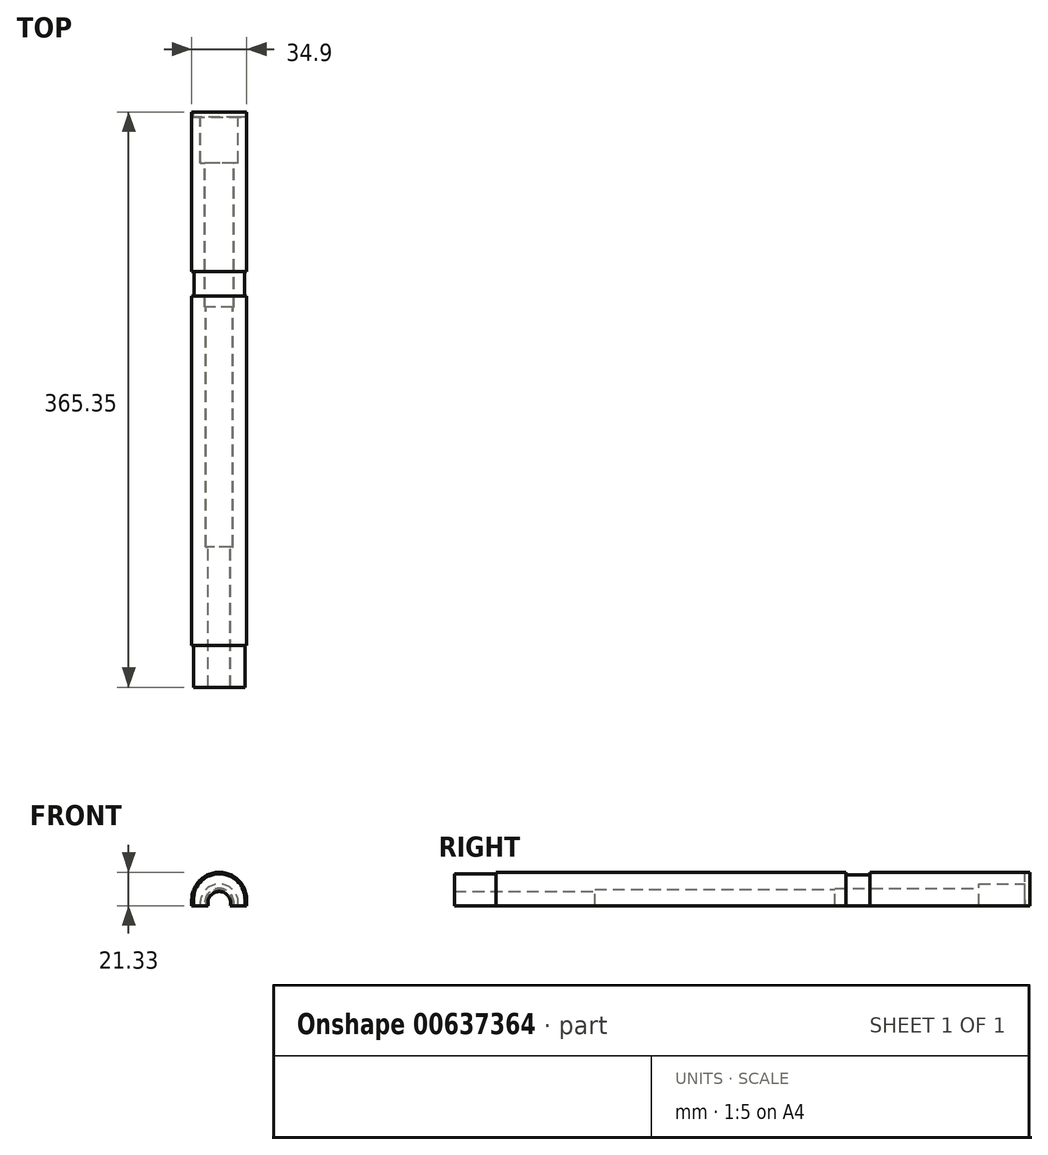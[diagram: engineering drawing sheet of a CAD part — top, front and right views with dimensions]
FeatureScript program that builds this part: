
annotation { "Feature Type Name" : "Feature", "Feature Type Description" : "" }
export const myFeature = defineFeature(function(context is Context, id is Id, definition is map)
    precondition{}
    {
        {
            var Q0;
            Q0=qCreatedBy(makeId("Front.planeOp"),FACE);
            var sketch = newSketch(context, id + "F0", { "sketchPlane" : qUnion([Q0])});
            skLineSegment(sketch, "E0", {"start": v(17.45, -4.64) * mm, "end": v(11.93, -4.64) * mm});
            skLineSegment(sketch, "E1.trimOffspring", {"start": v(-11.93, -4.64) * mm, "end": v(-17.45, -4.64) * mm});
            skLineSegment(sketch, "E2.MirrorCS", {"start": v(17.45, -4.64) * mm, "end": v(17.45, -0.86) * mm});
            skArc(sketch, "E3", {"start": v(17.45, -0.86) * mm, "mid": v(0, 16.7) * mm, "end": v(-17.45, -0.86) * mm});
            skLineSegment(sketch, "E4", {"start": v(-17.45, -0.86) * mm, "end": v(-17.45, -4.64) * mm});
            skArc(sketch, "E5", {"start": v(11.93, -4.64) * mm, "mid": v(0, 9.2) * mm, "end": v(-11.93, -4.64) * mm});
            skSolve(sketch);
        }
        {
            var Q0;
            Q0=makeQuery(id+"F0.imprint","IMPRINT",FACE,{"disambiguationData":[TD([[makeQuery(id+"F0.imprint","IMPRINT",EDGE,{"derivedFrom":sQuery(id+"F0.wireOp",EDGE,"E0")}),-1.0]])]});
            extrude(context, id + "F1", {"entities" : qUnion([Q0]), "depth" : 29.2 * mm, "offsetDistance" : 25.4 * mm});
        }
        {
            var Q0;
            Q0=makeQuery(id+"F1.opExtrude","CAP_FACE",FACE,{"disambiguationData":[OSD([sQuery(id+"F0.wireOp",EDGE,"E0"),sQuery(id+"F0.wireOp",EDGE,"E1.trimOffspring"),sQuery(id+"F0.wireOp",EDGE,"E2.MirrorCS"),sQuery(id+"F0.wireOp",EDGE,"E3"),sQuery(id+"F0.wireOp",EDGE,"E4"),sQuery(id+"F0.wireOp",EDGE,"E5")])],"isStart":false});
            var sketch = newSketch(context, id + "F2", { "sketchPlane" : qUnion([Q0])});
            skArc(sketch, "E6", {"start": v(9.11, -4.64) * mm, "mid": v(0, 6.5) * mm, "end": v(-9.11, -4.64) * mm});
            skLineSegment(sketch, "E7", {"start": v(-17.45, -4.64) * mm, "end": v(-9.11, -4.64) * mm});
            skLineSegment(sketch, "E8", {"start": v(-17.45, -0.86) * mm, "end": v(-17.45, -4.64) * mm});
            skLineSegment(sketch, "E9", {"start": v(17.45, -0.86) * mm, "end": v(17.45, -4.64) * mm});
            skLineSegment(sketch, "E10", {"start": v(17.45, -4.64) * mm, "end": v(9.11, -4.64) * mm});
            skArc(sketch, "E11", {"start": v(17.45, -0.86) * mm, "mid": v(0, 16.7) * mm, "end": v(-17.45, -0.86) * mm});
            skSolve(sketch);
        }
        {
            var Q0;
            {var subQ0=sQuery(id+"F2.wireOp",EDGE,"E6");Q0=makeQuery(id+"F2.imprint","IMPRINT",FACE,{"disambiguationData":[TD([[makeQuery(id+"F2.imprint","IMPRINT",EDGE,{"derivedFrom":subQ0}),-1.0]])]});}
            var Q1;
            {var subQ1=sQuery(id+"F2.wireOp",EDGE,"E8");Q1=makeQuery(id+"F2.imprint","IMPRINT",FACE,{"disambiguationData":[TD([[makeQuery(id+"F2.imprint","IMPRINT",EDGE,{"derivedFrom":subQ1}),1.0]])]});}
            extrude(context, id + "F3", {"entities" : qUnion([Q0, Q1]), "operationType" : NewBodyOperationType.ADD, "depth" : 69.06 * mm, "offsetDistance" : 25.4 * mm});
        }
        {
            var Q0;
            Q0=makeQuery(id+"F3.opExtrude","CAP_FACE",FACE,{"disambiguationData":[OSD([sQuery(id+"F2.wireOp",EDGE,"E6"),sQuery(id+"F2.wireOp",EDGE,"E7"),sQuery(id+"F2.wireOp",EDGE,"E8"),sQuery(id+"F2.wireOp",EDGE,"E9"),sQuery(id+"F2.wireOp",EDGE,"E10"),sQuery(id+"F2.wireOp",EDGE,"E11")])],"isStart":false});
            var sketch = newSketch(context, id + "F4", { "sketchPlane" : qUnion([Q0])});
            skArc(sketch, "E12.0", {"start": v(15.93, -0.85) * mm, "mid": v(0, 15.17) * mm, "end": v(-15.93, -0.85) * mm});
            skLineSegment(sketch, "E13", {"start": v(15.93, -0.85) * mm, "end": v(15.93, -4.64) * mm});
            skLineSegment(sketch, "E14", {"start": v(-15.93, -0.85) * mm, "end": v(-15.9, -4.64) * mm});
            skLineSegment(sketch, "E15", {"start": v(9.11, -4.64) * mm, "end": v(15.93, -4.64) * mm});
            skLineSegment(sketch, "E16", {"start": v(-9.11, -4.64) * mm, "end": v(-15.9, -4.64) * mm});
            skSolve(sketch);
        }
        {
            var Q0;
            Q0=makeQuery(id+"F4.imprint","IMPRINT",FACE,{"disambiguationData":[TD([[makeQuery(id+"F4.imprint","IMPRINT",EDGE,{"derivedFrom":sQuery(id+"F4.wireOp",EDGE,"E12.0")}),1.0]])]});
            extrude(context, id + "F5", {"entities" : qUnion([Q0]), "operationType" : NewBodyOperationType.ADD, "depth" : 15.42 * mm, "offsetDistance" : 25.4 * mm});
        }
        {
            var Q0;
            Q0=makeQuery(id+"F5.opExtrude","CAP_FACE",FACE,{"disambiguationData":[OSD([sQuery(id+"F2.wireOp",EDGE,"E6"),sQuery(id+"F4.wireOp",EDGE,"E12.0"),sQuery(id+"F4.wireOp",EDGE,"E13"),sQuery(id+"F4.wireOp",EDGE,"E14"),sQuery(id+"F4.wireOp",EDGE,"E15"),sQuery(id+"F4.wireOp",EDGE,"E16")])],"isStart":false});
            var sketch = newSketch(context, id + "F6", { "sketchPlane" : qUnion([Q0])});
            skArc(sketch, "E17", {"start": v(9.11, -4.64) * mm, "mid": v(0, 6.5) * mm, "end": v(-9.11, -4.64) * mm});
            skLineSegment(sketch, "E18", {"start": v(-17.45, -4.64) * mm, "end": v(-9.11, -4.64) * mm});
            skLineSegment(sketch, "E19", {"start": v(-17.45, -0.86) * mm, "end": v(-17.45, -4.64) * mm});
            skLineSegment(sketch, "E20", {"start": v(17.45, -0.86) * mm, "end": v(17.45, -4.64) * mm});
            skLineSegment(sketch, "E21", {"start": v(17.45, -4.64) * mm, "end": v(9.11, -4.64) * mm});
            skArc(sketch, "E22", {"start": v(17.45, -0.86) * mm, "mid": v(0, 16.7) * mm, "end": v(-17.45, -0.86) * mm});
            skSolve(sketch);
        }
        {
            var Q0;
            {var subQ1=sQuery(id+"F6.wireOp",EDGE,"E17");Q0=makeQuery(id+"F6.imprint","IMPRINT",FACE,{"disambiguationData":[TD([[makeQuery(id+"F6.imprint","IMPRINT",EDGE,{"derivedFrom":subQ1}),-1.0]])]});}
            var Q1;
            {var subQ3=sQuery(id+"F6.wireOp",EDGE,"E19");Q1=makeQuery(id+"F6.imprint","IMPRINT",FACE,{"disambiguationData":[TD([[makeQuery(id+"F6.imprint","IMPRINT",EDGE,{"derivedFrom":subQ3}),1.0]])]});}
            extrude(context, id + "F7", {"entities" : qUnion([Q0, Q1]), "operationType" : NewBodyOperationType.ADD, "depth" : 6.96 * mm, "offsetDistance" : 25.4 * mm});
        }
        {
            var Q0;
            Q0=makeQuery(id+"F7.opExtrude","CAP_FACE",FACE,{"disambiguationData":[OSD([sQuery(id+"F6.wireOp",EDGE,"E17"),sQuery(id+"F6.wireOp",EDGE,"E18"),sQuery(id+"F6.wireOp",EDGE,"E19"),sQuery(id+"F6.wireOp",EDGE,"E20"),sQuery(id+"F6.wireOp",EDGE,"E21"),sQuery(id+"F6.wireOp",EDGE,"E22")])],"isStart":false});
            var sketch = newSketch(context, id + "F8", { "sketchPlane" : qUnion([Q0])});
            skLineSegment(sketch, "E23", {"start": v(-17.45, -0.86) * mm, "end": v(-17.45, -4.64) * mm});
            skLineSegment(sketch, "E24", {"start": v(17.45, -0.86) * mm, "end": v(17.45, -4.64) * mm});
            skArc(sketch, "E25", {"start": v(17.45, -0.86) * mm, "mid": v(0, 16.7) * mm, "end": v(-17.45, -0.86) * mm});
            skLineSegment(sketch, "E26", {"start": v(-17.45, -4.64) * mm, "end": v(-8.44, -4.64) * mm});
            skLineSegment(sketch, "E27.trimOffspring", {"start": v(8.44, -4.64) * mm, "end": v(17.45, -4.64) * mm});
            skArc(sketch, "E28", {"start": v(8.44, -4.64) * mm, "mid": v(0, 5.84) * mm, "end": v(-8.44, -4.64) * mm});
            skSolve(sketch);
        }
        {
            var Q0;
            {var subQ1=sQuery(id+"F8.wireOp",EDGE,"E23");Q0=makeQuery(id+"F8.imprint","IMPRINT",FACE,{"disambiguationData":[TD([[makeQuery(id+"F8.imprint","IMPRINT",EDGE,{"derivedFrom":subQ1}),1.0]])]});}
            var Q1;
            {var subQ2=sQuery(id+"F8.wireOp",EDGE,"E28");Q1=makeQuery(id+"F8.imprint","IMPRINT",FACE,{"disambiguationData":[TD([[makeQuery(id+"F8.imprint","IMPRINT",EDGE,{"derivedFrom":subQ2}),-1.0]])]});}
            extrude(context, id + "F9", {"entities" : qUnion([Q0, Q1]), "operationType" : NewBodyOperationType.ADD, "depth" : 152.4 * mm, "offsetDistance" : 25.4 * mm});
        }
        {
            var Q0;
            Q0=makeQuery(id+"F9.opExtrude","CAP_FACE",FACE,{"disambiguationData":[OSD([sQuery(id+"F8.wireOp",EDGE,"E23"),sQuery(id+"F8.wireOp",EDGE,"E24"),sQuery(id+"F8.wireOp",EDGE,"E25"),sQuery(id+"F8.wireOp",EDGE,"E26"),sQuery(id+"F8.wireOp",EDGE,"3393e5be-c0de-4e0d-a7a5-b845585d77bd.converted"),sQuery(id+"F8.wireOp",EDGE,"E27.trimOffspring")])],"isStart":false});
            var sketch = newSketch(context, id + "F10", { "sketchPlane" : qUnion([Q0])});
            skLineSegment(sketch, "E29", {"start": v(-17.45, -0.86) * mm, "end": v(-17.45, -4.64) * mm});
            skLineSegment(sketch, "E30", {"start": v(17.45, -0.86) * mm, "end": v(17.45, -4.64) * mm});
            skArc(sketch, "E31", {"start": v(17.45, -0.86) * mm, "mid": v(0, 16.7) * mm, "end": v(-17.45, -0.86) * mm});
            skLineSegment(sketch, "E32", {"start": v(-17.45, -4.64) * mm, "end": v(-7, -4.64) * mm});
            skArc(sketch, "E33.converted", {"start": v(7, -4.64) * mm, "mid": v(0, 4.44) * mm, "end": v(-7, -4.64) * mm});
            skLineSegment(sketch, "E34.trimOffspring", {"start": v(7, -4.64) * mm, "end": v(17.45, -4.64) * mm});
            skSolve(sketch);
        }
        {
            var Q0;
            Q0=makeQuery(id+"F10.imprint","IMPRINT",FACE,{"disambiguationData":[TD([[makeQuery(id+"F10.imprint","IMPRINT",EDGE,{"derivedFrom":sQuery(id+"F10.wireOp",EDGE,"E29")}),1.0]])]});
            var Q1;
            {var subQ2=sQuery(id+"F10.wireOp",EDGE,"E33.converted");Q1=makeQuery(id+"F10.imprint","IMPRINT",FACE,{"disambiguationData":[TD([[makeQuery(id+"F10.imprint","IMPRINT",EDGE,{"derivedFrom":subQ2}),-1.0]])]});}
            extrude(context, id + "F11", {"entities" : qUnion([Q0, Q1]), "operationType" : NewBodyOperationType.ADD, "depth" : 89.15 * mm, "offsetDistance" : 25.4 * mm});
        }
        {
            var Q0;
            Q0=makeQuery(id+"F11.opExtrude","CAP_FACE",FACE,{"disambiguationData":[OSD([sQuery(id+"F10.wireOp",EDGE,"E29"),sQuery(id+"F10.wireOp",EDGE,"E30"),sQuery(id+"F10.wireOp",EDGE,"E31"),sQuery(id+"F10.wireOp",EDGE,"E32"),sQuery(id+"F10.wireOp",EDGE,"E33.converted"),sQuery(id+"F10.wireOp",EDGE,"E34.trimOffspring")])],"isStart":false});
            var sketch = newSketch(context, id + "F12", { "sketchPlane" : qUnion([Q0])});
            skArc(sketch, "E35.0", {"start": v(16.43, -0.86) * mm, "mid": v(0, 15.68) * mm, "end": v(-16.43, -0.86) * mm});
            skLineSegment(sketch, "E36.0", {"start": v(16.43, -4.64) * mm, "end": v(16.43, -0.86) * mm});
            skLineSegment(sketch, "E37.0", {"start": v(-16.43, -0.86) * mm, "end": v(-16.43, -4.64) * mm});
            skLineSegment(sketch, "E38", {"start": v(-17.45, -0.86) * mm, "end": v(-17.45, -4.64) * mm});
            skLineSegment(sketch, "E39", {"start": v(-16.43, -4.64) * mm, "end": v(-17.45, -4.64) * mm});
            skLineSegment(sketch, "E40", {"start": v(16.43, -4.64) * mm, "end": v(17.45, -4.64) * mm});
            skLineSegment(sketch, "E41", {"start": v(17.45, -4.64) * mm, "end": v(17.45, -0.86) * mm});
            skArc(sketch, "E42", {"start": v(17.45, -0.86) * mm, "mid": v(0, 16.7) * mm, "end": v(-17.45, -0.86) * mm});
            skSolve(sketch);
        }
        {
            var Q0;
            Q0=makeQuery(id+"F12.imprint","IMPRINT",FACE,{"disambiguationData":[TD([[makeQuery(id+"F12.imprint","IMPRINT",EDGE,{"derivedFrom":sQuery(id+"F12.wireOp",EDGE,"E35.0")}),-1.0]])]});
            extrude(context, id + "F13", {"entities" : qUnion([Q0]), "operationType" : NewBodyOperationType.REMOVE, "oppositeDirection" : true, "depth" : 26.5 * mm, "offsetDistance" : 25.4 * mm});
        }
        {
            var Q0;
            Q0=makeQuery(id+"F1.opExtrude","CAP_FACE",FACE,{"disambiguationData":[OSD([sQuery(id+"F0.wireOp",EDGE,"E0"),sQuery(id+"F0.wireOp",EDGE,"E1.trimOffspring"),sQuery(id+"F0.wireOp",EDGE,"E2.MirrorCS"),sQuery(id+"F0.wireOp",EDGE,"E3"),sQuery(id+"F0.wireOp",EDGE,"E4"),sQuery(id+"F0.wireOp",EDGE,"E5")])],"isStart":true});
            var sketch = newSketch(context, id + "F14", { "sketchPlane" : qUnion([Q0])});
            skArc(sketch, "E43.0", {"start": v(-16.69, -0.86) * mm, "mid": v(0, 15.93) * mm, "end": v(16.69, -0.86) * mm});
            skLineSegment(sketch, "E44", {"start": v(16.69, -0.86) * mm, "end": v(16.67, -4.64) * mm});
            skLineSegment(sketch, "E45", {"start": v(-16.69, -0.86) * mm, "end": v(-16.69, -4.64) * mm});
            skLineSegment(sketch, "E46", {"start": v(16.67, -4.64) * mm, "end": v(11.93, -4.64) * mm});
            skLineSegment(sketch, "E47", {"start": v(-16.69, -4.64) * mm, "end": v(-11.93, -4.64) * mm});
            skArc(sketch, "E48", {"start": v(11.93, -4.64) * mm, "mid": v(0, 9.2) * mm, "end": v(-11.93, -4.64) * mm});
            skSolve(sketch);
        }
        {
            var Q0;
            Q0=makeQuery(id+"F14.imprint","IMPRINT",FACE,{"disambiguationData":[TD([[makeQuery(id+"F14.imprint","IMPRINT",EDGE,{"derivedFrom":sQuery(id+"F14.wireOp",EDGE,"E43.0")}),-1.0]])]});
            extrude(context, id + "F15", {"entities" : qUnion([Q0]), "operationType" : NewBodyOperationType.ADD, "depth" : 3.15 * mm, "offsetDistance" : 25.4 * mm});
        }
    });
